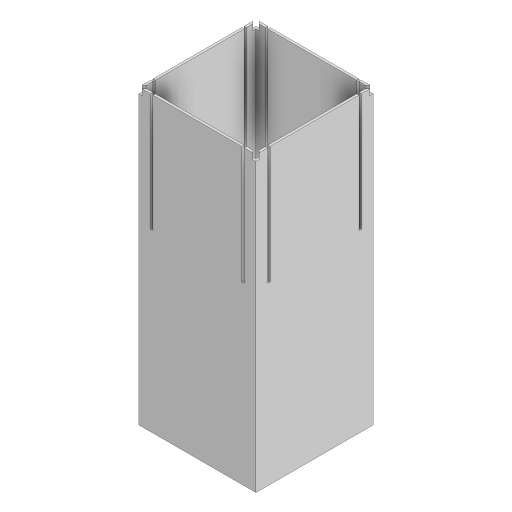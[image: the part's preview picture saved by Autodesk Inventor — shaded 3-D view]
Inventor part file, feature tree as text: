
AUTODESK INVENTOR PART (.ipt)
format: ipt  version: 2024.3 (Build 283343000, 343)  size: 293,888 bytes
history: native  units: mm
features: extrude x5, sketch x5, mirror x2, plane x2
ambient origin geometry x8: Origin, YZ Plane, XZ Plane, XY Plane, X Axis, Y Axis, Z Axis, Center Point
bodies: Solid1 (feature_tree)
feature tree (14):
  extrude  "Extrusion1"  Depth=100.0mm
  extrude  "Extrusion3"  Depth=250.0mm TaperAngle=0.0deg
  mirror  "Mirror2"
  extrude  "Extrusion4"  Depth=2.0mm
  mirror  "Mirror3"
  plane  "Work Plane1"
  sketch  "Sketch5"  dims[d11=10.0mm d12=220.0mm d13=0.0mm]
  extrude  "Extrusion5"  Depth=10.0mm TaperAngle=0.0deg
  plane  "Work Plane2"
  extrude  "Extrusion6"  Depth=2.0mm
  sketch  "Sketch1"  dims[d0=100.0mm d1=100.0mm]
  sketch  "Sketch3"  dims[d2=2.0mm d3=250.0mm d4=0.0mm]
  sketch  "Sketch4"  dims[d9=100.0mm d10=2.0mm]
  sketch  "Sketch6"  dims[d14=10.0mm d15=2.0mm d16=100.0mm d17=0.0mm d18=220.0mm d19=0.0mm d20=5.0mm d21=4.0mm d22=0.0mm d23=0.0mm d24=220.0mm d25=0.0mm d26=4.0mm d27=5.0mm d28=0.0mm d29=220.0mm d30=0.0mm]
